# Revit family: Geberit Duofix element za izlivno korito, 175 cm, sa Delta ugradnim vodokotlićem 12 cm, predzidna armatura_PRO_255085
name_source: partatom
category: Plumbing Fixtures
revit_build: Autodesk Revit 2018 (Build: 20190510_1515(x64)
units: mm (PartAtom-declared; Revit-internal decimal feet)

## family parameters
Always vertical = Yes
Cut with Voids When Loaded = No
OmniClass Number = 23.45.05.00
OmniClass Title = Sanitary Equipment
Part Type = Normal
Room Calculation Point = Yes
Round Connector Dimension = Use Diameter
Shared = No
Work Plane-Based = No

## types (1)
- 111.569.00.1 Geberit Duofix element za izlivno korito, 175 cm, sa Delta ugradnim vodokotlićem 12 cm, predzidna armatura
    ATT_10767 = 0.1 L/s
    BIM datoteka, datum izmene = 2021.12.01
    BIM datoteka, proizvođač = Geberit
    BIM datoteka, verzija = GEB MG 1.5
    Broj artikla = 111.569.00.1
    CW Connection = Yes
    D = 150 mm  [stored 0.492126 ft]
    D1 = 60 mm  [stored 0.19685 ft]
    Description = Geberit Duofix element za izlivno korito, 175 cm, sa Delta ugradnim vodokotlićem 12 cm, predzidna armatura
    EAN code basic data = 4025416857198
    Fabrički podešena količina ispiranja = 6 i 3 l
    GEB_culture = sr-RS
    GEB_generic_description = concealed cistern support frame for sink
    GEB_generic_manufacturer = generic
    GEB_imperial_engineering = No
    GEB_metric_engineering = Yes
    GEB_pimversion = 22.02.12
    GEB_processing_type = T
    GEB_reference = PRO_255085
    GEB_translations = {"ATT_10673":"EAN code basic data","ATT_10807":"Opseg podešavanje veće količine vode za ispiranje","ATT_10811":"Opseg podešavanja manje količine vode za ispiranje","ATT_10866":"Fabrički podešena količina ispiranja","applicationPurposes":"Namene","application_range":"Oblast primene","brandName":"Robna marka","characteristics":"Svojstva","connection_description1":"Opis priključka 1","connection_description2":"Opis priključka 2","GEB_connection_diameter1":"Prečnik priključka 1","GEB_connection_diameter2":"Prečnik priključka 2","connection_type_c01":"Vrsta priključka kod priključka 01","connection_type_c02":"Vrsta priključka kod priključka 02","content_creator":"BIM datoteka, proizvođač","content_date_changed":"BIM datoteka, datum izmene","content_version":"BIM datoteka, verzija","key 1000":"Broj artikla","name":"Naziv","productBrand":"Robna marka proizvoda","scopeOfDelivery":"Obim isporuke","type":"Tip","GEB_cut_length_c01":"Maksimalno skraćenje kod priključka 01","angle":"ugao","placement finished floor":"Na gornjoj ivici gotovog poda","rod spacing 180mm":"Razmak kačenja 180 mm","rod spacing 230mm":"Razmak kačenja 230 mm","sanitary socket":"Spojnica za prelaz","surface height":"Visina debljine poda","warning":"Upozorenje","fixed_material":"Osnovni materijal","fixed_material_01":"Osnovni materijal 01","fixed_material_02":"Osnovni materijal 02","fixed_material_03":"Osnovni materijal 03","fixed_material_04":"Osnovni materijal 04"}
    GEB_use_DN = Yes
    H = 1750 mm  [stored 5.74147 ft]
    H1 = 400 mm  [stored 1.31234 ft]
    H2 = 500 mm  [stored 1.64042 ft]
    H3 = 1630 mm  [stored 5.34777 ft]
    H4 = 1150 mm
    HW Connection = No
    IfcDescription = Geberit Duofix element za izlivno korito, 175 cm, sa Delta ugradnim vodokotlićem 12 cm, predzidna armatura
    IfcExportAs = IfcSanitaryTerminal
    IfcExportType = CISTERN
    LOD300 = No
    LOD400 = Yes
    Manufacturer = Geberit
    Namene = Za suvu gradnju
Za ugradnju u predzidne konstrukcije delimične ili visine etaže
Za ugradnju u instalacione zidove u visini etaže
Za ugradnju u jednoslojne suvomontažne zidove
Za montažu pljuvaonica Publica sa zidnom slavinom
Za montažu Geberit Publica izlivnog korita sa zidnom slavinom
Za armature na zidovima
Za jednokoličinsko, dvokoličinsko ili start/stop ispiranje
Za debljine poda 0–20 cm
    Naziv = Geberit Duofix element za izlivno korito, 175 cm, sa Delta ugradnim vodokotlićem 12 cm, predzidna armatura
    Obim isporuke = Ugaoni ventil R 1/2", kompatibilan sa MF adapterom, sa priključnim prstenom
Građevinska zaštita za revizioni otvor, od polistiren pene
4 zidna sidra
2 zaštitna čepa
Priključni set za WC, ø 90 mm
Priključno koleno 90° od PVC, ø 90 / 100 mm
6 sidra za veće terete M8
2 navojne šipke M12
Materijal za pričvršćivanje
    Oblast primene = sanitary systems
    Opis priključka 1 = cold water in
    Opis priključka 2 = sanitary out
    Opseg podešavanja manje količine vode za ispiranje = 3-4 l
    Opseg podešavanje veće količine vode za ispiranje = 4.5 / 6 / 7.5 l
    Osnovni materijal = Geberit, Plastic, Opaque white
    Osnovni materijal 01 = Geberit, Steel, Paint Finish, Blue
    Osnovni materijal 02 = Geberit, Laminate, Ivory, Matte
    Osnovni materijal 03 = Geberit, Steel, galvanized
    Osnovni materijal 04 = Geberit, PE-HD, Black
    Prečnik priključka 1 = 15 mm  [stored 0.0492126 ft]
    Prečnik priključka 2 = 90 mm  [stored 0.295276 ft]
    Robna marka = Geberit
    Robna marka proizvoda = Duofix
    Spojnica za prelaz = No
    Svojstva = Samonoseći okvir sa završnom obradom pečenim lakom
Okvir podeljen na dva dela
Okvir gore, otvoren
Okvir sa rupama ø 9 mm za učvršćenje u konstrukciji od drvenih okvira
Okvir sa prihvatnim otvorima za Geberit Duofix zidno sidro za elemente sa otvorenim okvirom gore
Potporne noge pocinkovane
Potporne noge, podesive od 0–20 cm
Sa velikim pločama stope, za veće uvođenje snage u pod
Priključno koleno koje se može montirati bez alata na različitim dubinama, opseg podešavanja 45 mm
Učvršćenje priključnog kolena, zvučno izolovano
Ugradni vodokotlić sa aktiviranjem sa prednje strane
Ugradni vodokotlić sa izolacijom protiv kondenzacije
Kod fabričkog podešavanja moguće je automatsko naknadno ispiranje
Priključak za vodu, pozadi ili gore na sredini
Traverza za armaturne priključke, pocinkovana
Traverza armaturnog priključka podesiva po visini
    Vent Connection = No
    Vrsta priključka kod priključka 01 = Rp½''
    Vrsta priključka kod priključka 02 = DN90/ø90 Spigot
    W = 500 mm  [stored 1.64042 ft]
    Waste Connection = Yes
    Z2_calculated = 226 mm  [stored 0.74147 ft]
    angle_cw = 90.00°
    button_depth = 115 mm  [stored 0.377297 ft]
    cistern_front_offset = 21 mm  [stored 0.0688976 ft]
    cistern_width = 420 mm  [stored 1.37795 ft]
    connection_bend = Yes
    cw_orientation = 1
    cw_pos = 200 mm  [stored 0.656168 ft]
    frame_btm = 1669 mm  [stored 5.47572 ft]
    h1 = 504 mm  [stored 1.65354 ft]
    outlet_flow = 0.0 L/s
    rod_width_180 = 180 mm  [stored 0.590551 ft]
    rod_width_230 = 230 mm  [stored 0.754593 ft]
    supply_connection_warning = Reducer connected to element not required and should not be accounted for in a BOM
    wt_h = 43 mm  [stored 0.141076 ft]

note: [stored X ft] marks values corroborated as IEEE doubles in the binary element streams (Revit-internal decimal feet)

## geometry (parser evidence)
native form markers: Blend x6, Sweep x4
no freeform markers — native parametric forms only
